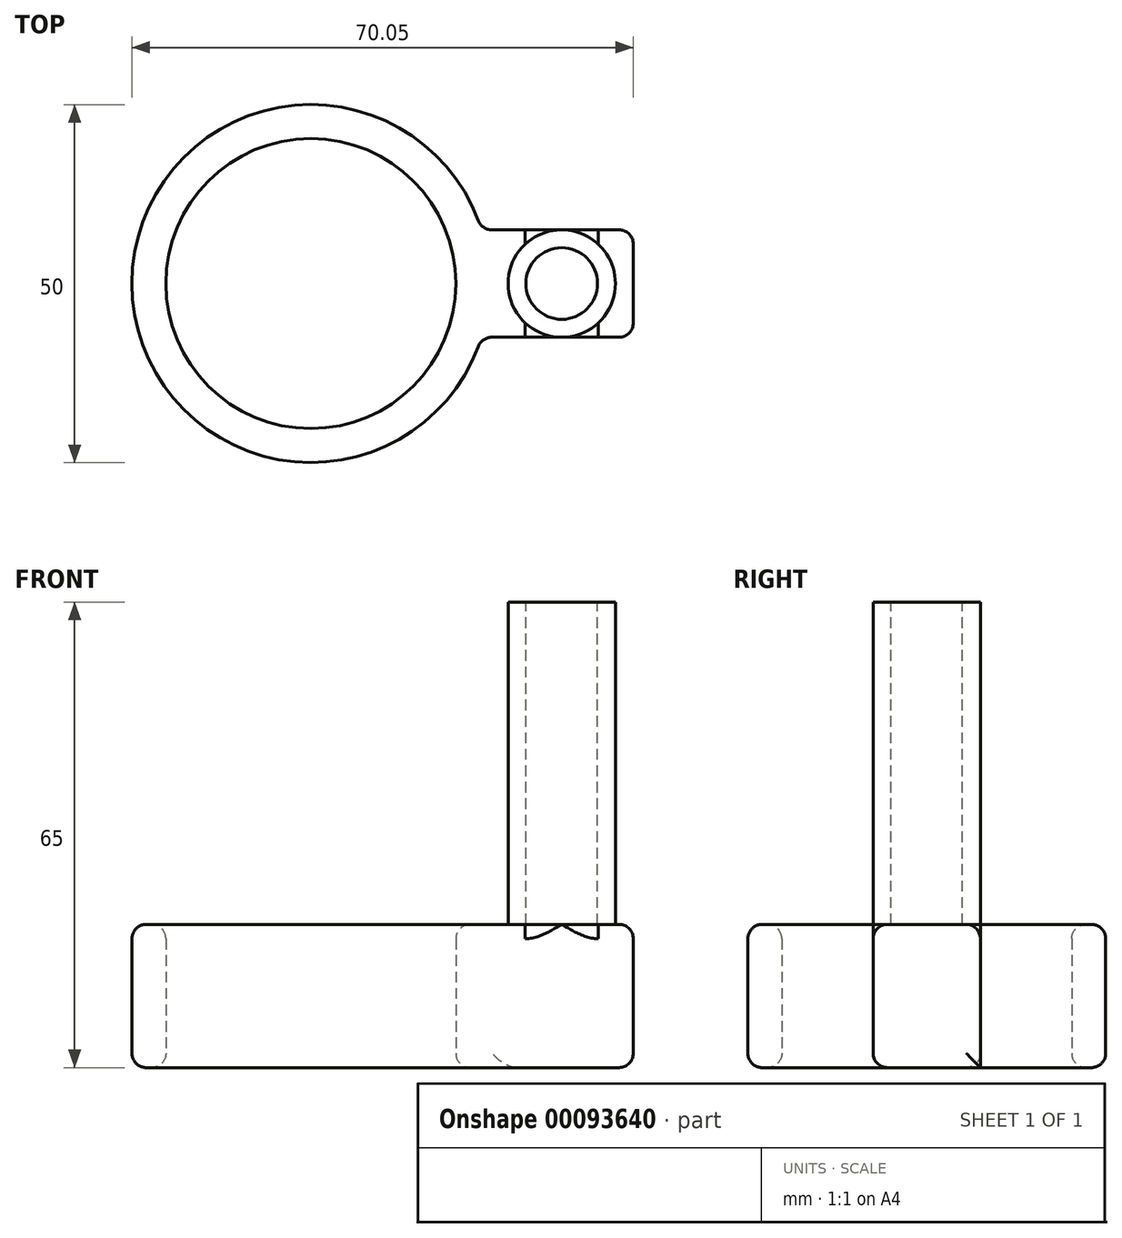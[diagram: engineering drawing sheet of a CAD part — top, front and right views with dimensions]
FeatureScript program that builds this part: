
annotation { "Feature Type Name" : "Feature", "Feature Type Description" : "" }
export const myFeature = defineFeature(function(context is Context, id is Id, definition is map)
    precondition{}
    {
        {
            var Q0;
            Q0=qCreatedBy(makeId("Top.planeOp"),FACE);
            var sketch = newSketch(context, id + "F0", { "sketchPlane" : qUnion([Q0])});
            skCircle(sketch, "E0", {"center": v(0, 0) * mm, "radius": 20.25 * mm});
            skArc(sketch, "E1", {"start": v(23.85, 7.5) * mm, "mid": v(-25, 0) * mm, "end": v(23.85, -7.5) * mm});
            skLineSegment(sketch, "E2.bottom", {"start": v(23.85, 7.5) * mm, "end": v(45.05, 7.5) * mm});
            skLineSegment(sketch, "E2.top", {"start": v(23.85, -7.5) * mm, "end": v(45.05, -7.5) * mm});
            skLineSegment(sketch, "E2.right", {"start": v(45.05, 7.5) * mm, "end": v(45.05, -7.5) * mm});
            skSolve(sketch);
        }
        {
            var Q0;
            Q0=makeQuery(id+"F0.imprint","IMPRINT",FACE,{"disambiguationData":[TD([[makeQuery(id+"F0.imprint","IMPRINT",EDGE,{"derivedFrom":sQuery(id+"F0.wireOp",EDGE,"E0")}),-1.0]])]});
            extrude(context, id + "F1", {"entities" : qUnion([Q0]), "depth" : 20 * mm});
        }
        {
            var Q0;
            Q0=makeQuery(id+"F1.opExtrude","CAP_FACE",FACE,{"disambiguationData":[OSD([sQuery(id+"F0.wireOp",EDGE,"E0"),sQuery(id+"F0.wireOp",EDGE,"E1"),sQuery(id+"F0.wireOp",EDGE,"E2.bottom"),sQuery(id+"F0.wireOp",EDGE,"E2.top"),sQuery(id+"F0.wireOp",EDGE,"E2.right")])],"isStart":false});
            var sketch = newSketch(context, id + "F2", { "sketchPlane" : qUnion([Q0])});
            skCircle(sketch, "E3", {"center": v(35.05, 0) * mm, "radius": 5 * mm});
            skCircle(sketch, "E4", {"center": v(35.05, 0) * mm, "radius": 7.5 * mm});
            skSolve(sketch);
        }
        {
            var Q0;
            Q0=makeQuery(id+"F2.imprint","IMPRINT",FACE,{"disambiguationData":[TD([[makeQuery(id+"F2.imprint","IMPRINT",EDGE,{"derivedFrom":sQuery(id+"F2.wireOp",EDGE,"E3")}),1.0]])]});
            var Q1;
            Q1=makeQuery(id+"F2.imprint","IMPRINT",FACE,{"disambiguationData":[TD([[makeQuery(id+"F2.imprint","IMPRINT",EDGE,{"derivedFrom":sQuery(id+"F2.wireOp",EDGE,"E3")}),-1.0]])]});
            extrude(context, id + "F3", {"entities" : qUnion([Q0, Q1]), "operationType" : NewBodyOperationType.ADD, "depth" : 45 * mm});
        }
        {
            var Q0;
            Q0=makeQuery(id+"F3.opExtrude","CAP_FACE",FACE,{"disambiguationData":[OSD([sQuery(id+"F2.wireOp",EDGE,"E4")])],"isStart":false});
            var sketch = newSketch(context, id + "F4", { "sketchPlane" : qUnion([Q0])});
            skCircle(sketch, "E5", {"center": v(35.05, 0) * mm, "radius": 5 * mm});
            skSolve(sketch);
        }
        {
            var Q0;
            Q0=makeQuery(id+"F4.imprint","IMPRINT",FACE,{"disambiguationData":[TD([[makeQuery(id+"F4.imprint","IMPRINT",EDGE,{"derivedFrom":sQuery(id+"F4.wireOp",EDGE,"E5")}),1.0]])]});
            extrude(context, id + "F5", {"entities" : qUnion([Q0]), "operationType" : NewBodyOperationType.REMOVE, "oppositeDirection" : true, "depth" : 45 * mm});
        }
        {
            var Q0;
            Q0=makeQuery(id+"F1.opExtrude","CAP_EDGE",EDGE,{"disambiguationData":[OSD([sQuery(id+"F0.wireOp",EDGE,"E0")])],"isStart":false});
            var Q1;
            Q1=makeQuery(id+"F1.opExtrude","CAP_EDGE",EDGE,{"disambiguationData":[OSD([sQuery(id+"F0.wireOp",EDGE,"E1")])],"isStart":false});
            var Q2;
            Q2=makeQuery(id+"F1.opExtrude","CAP_EDGE",EDGE,{"disambiguationData":[OSD([sQuery(id+"F0.wireOp",EDGE,"E0")])],"isStart":true});
            var Q3;
            Q3=makeQuery(id+"F1.opExtrude","CAP_EDGE",EDGE,{"disambiguationData":[OSD([sQuery(id+"F0.wireOp",EDGE,"E1")])],"isStart":true});
            var Q4;
            Q4=makeQuery(id+"F1.opExtrude","SWEPT_EDGE",EDGE,{"disambiguationData":[OSD([sQuery(id+"F0.wireOp",EDGE,"E1"),sQuery(id+"F0.wireOp",EDGE,"E2.top")])]});
            var Q5;
            Q5=makeQuery(id+"F1.opExtrude","CAP_EDGE",EDGE,{"disambiguationData":[OSD([sQuery(id+"F0.wireOp",EDGE,"E2.top")])],"isStart":true});
            var Q6;
            Q6=makeQuery(id+"F1.opExtrude","CAP_EDGE",EDGE,{"disambiguationData":[OSD([sQuery(id+"F0.wireOp",EDGE,"E2.right")])],"isStart":true});
            var Q7;
            Q7=makeQuery(id+"F1.opExtrude","SWEPT_EDGE",EDGE,{"disambiguationData":[OSD([sQuery(id+"F0.wireOp",EDGE,"E2.top"),sQuery(id+"F0.wireOp",EDGE,"E2.right")])]});
            var Q8;
            Q8=makeQuery(id+"F1.opExtrude","CAP_EDGE",EDGE,{"disambiguationData":[OSD([sQuery(id+"F0.wireOp",EDGE,"E2.right")])],"isStart":false});
            var Q9;
            {var subQ0=sQuery(id+"F0.wireOp",EDGE,"E2.right");var subQ1=sQuery(id+"F0.wireOp",EDGE,"E2.top");Q9=makeQuery(id+"F3.boolean.opBoolean","SPLIT",EDGE,{"disambiguationData":[TD([makeQuery(id+"F1.opExtrude","SWEPT_FACE",FACE,{"disambiguationData":[OSD([subQ0])]})])],"derivedFrom":makeQuery(id+"F1.opExtrude","CAP_EDGE",EDGE,{"disambiguationData":[OSD([subQ1])],"isStart":false})});}
            var Q10;
            {var subQ0=sQuery(id+"F0.wireOp",EDGE,"E2.top");var subQ1=sQuery(id+"F0.wireOp",EDGE,"E1");Q10=makeQuery(id+"F3.boolean.opBoolean","SPLIT",EDGE,{"disambiguationData":[TD([makeQuery(id+"F1.opExtrude","SWEPT_FACE",FACE,{"disambiguationData":[OSD([subQ1])]})])],"derivedFrom":makeQuery(id+"F1.opExtrude","CAP_EDGE",EDGE,{"disambiguationData":[OSD([subQ0])],"isStart":false})});}
            var Q11;
            {var subQ0=sQuery(id+"F0.wireOp",EDGE,"E2.right");var subQ1=sQuery(id+"F0.wireOp",EDGE,"E2.bottom");Q11=makeQuery(id+"F3.boolean.opBoolean","SPLIT",EDGE,{"disambiguationData":[TD([makeQuery(id+"F1.opExtrude","SWEPT_FACE",FACE,{"disambiguationData":[OSD([subQ0])]})])],"derivedFrom":makeQuery(id+"F1.opExtrude","CAP_EDGE",EDGE,{"disambiguationData":[OSD([subQ1])],"isStart":false})});}
            var Q12;
            Q12=makeQuery(id+"F1.opExtrude","SWEPT_EDGE",EDGE,{"disambiguationData":[OSD([sQuery(id+"F0.wireOp",EDGE,"E2.bottom"),sQuery(id+"F0.wireOp",EDGE,"E2.right")])]});
            var Q13;
            Q13=makeQuery(id+"F1.opExtrude","SWEPT_EDGE",EDGE,{"disambiguationData":[OSD([sQuery(id+"F0.wireOp",EDGE,"E1"),sQuery(id+"F0.wireOp",EDGE,"E2.bottom")])]});
            fillet(context, id + "F6", {"entities" : qUnion([Q0, Q1, Q2, Q3, Q4, Q5, Q6, Q7, Q8, Q9, Q10, Q11, Q12, Q13]), "radius" : 2 * mm, "tangentPropagation" : true, "allowEdgeOverflow" : false});
        }
    });
